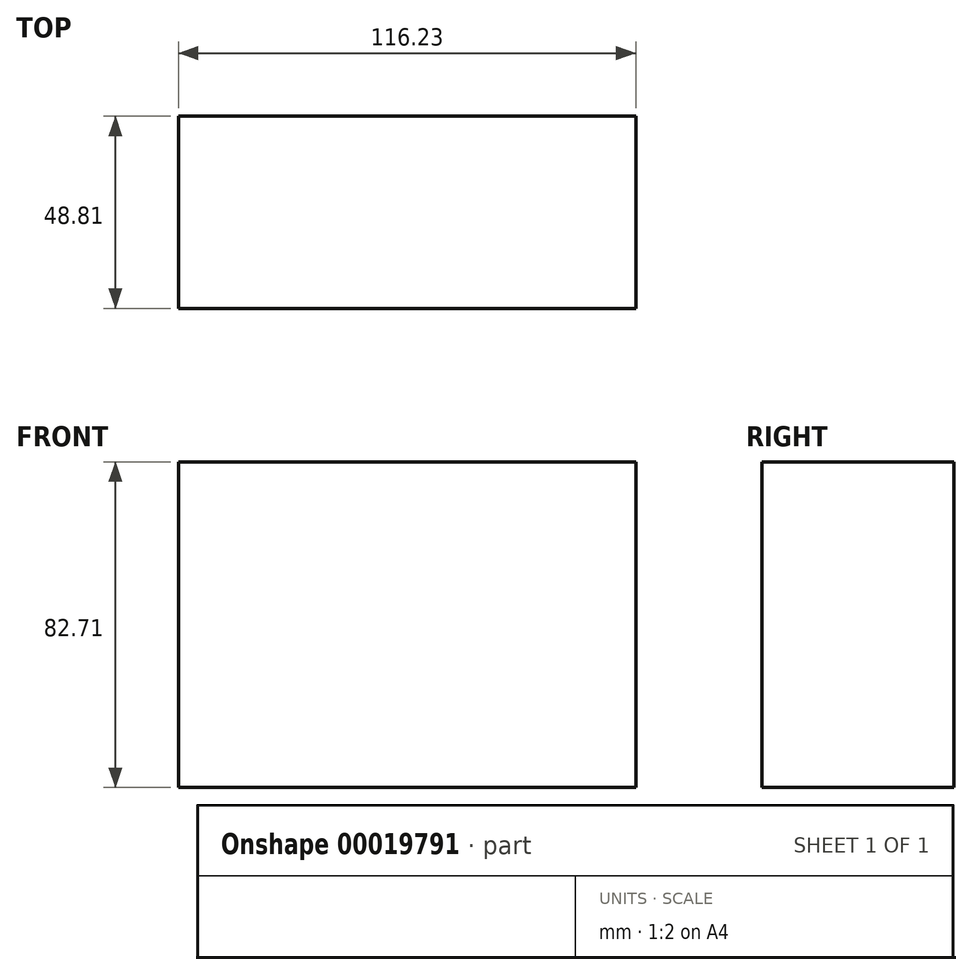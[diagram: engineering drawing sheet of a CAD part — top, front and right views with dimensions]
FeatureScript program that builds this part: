
annotation { "Feature Type Name" : "Feature", "Feature Type Description" : "" }
export const myFeature = defineFeature(function(context is Context, id is Id, definition is map)
    precondition{}
    {
        {
            var Q0;
            Q0=qCreatedBy(makeId("Top.planeOp"),FACE);
            var sketch = newSketch(context, id + "F0", { "sketchPlane" : qUnion([Q0])});
            skLineSegment(sketch, "E0.bottom", {"start": v(0, 2.31) * mm, "end": v(116.23, 2.31) * mm});
            skLineSegment(sketch, "E0.top", {"start": v(0, -46.5) * mm, "end": v(116.23, -46.5) * mm});
            skLineSegment(sketch, "E0.left", {"start": v(0, 2.31) * mm, "end": v(0, -46.5) * mm});
            skLineSegment(sketch, "E0.right", {"start": v(116.23, 2.31) * mm, "end": v(116.23, -46.5) * mm});
            skSolve(sketch);
        }
        {
            var Q0;
            Q0 = qSketchRegion(id + "F0", true);
            extrude(context, id + "F1", {"entities" : qUnion([Q0]), "depth" : 82.7 * mm});
        }
    });
